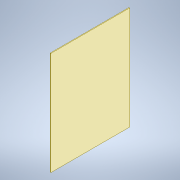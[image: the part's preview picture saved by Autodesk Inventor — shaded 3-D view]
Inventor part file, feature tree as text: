
AUTODESK INVENTOR PART (.ipt)
format: ipt  version: 2021 (Build 250183000, 183)  size: 89,088 bytes
history: native  units: mm
features: extrude x1, sketch x1
ambient origin geometry x8: Origin, YZ Plane, XZ Plane, XY Plane, X Axis, Y Axis, Z Axis, Center Point
bodies: Solid1 (feature_tree)
feature tree (2):
  extrude  "Extrusion1"  Depth=326.0mm
  sketch  "Sketch1"  dims[d0=427.0mm d1=326.0mm d2=3.0mm d3=0.0mm]
